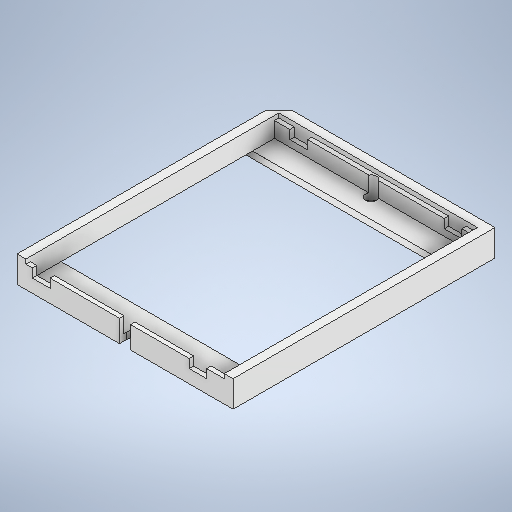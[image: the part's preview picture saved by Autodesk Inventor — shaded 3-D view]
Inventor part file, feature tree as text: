
AUTODESK INVENTOR PART (.ipt)
format: ipt  version: 2025 (Build 290162000, 162)  size: 386,560 bytes
history: native  units: in
note: dims shown in document units (in); Inventor stores cm internally (conversion verified against a paired STEP export)
features: extrude x11, sketch x10
ambient origin geometry x8: Origin, YZ Plane, XZ Plane, XY Plane, X Axis, Y Axis, Z Axis, Center Point
bodies: Solid1 (feature_tree)
feature tree (21):
  extrude  "Extrusion1"  Depth=1.9331in
  extrude  "Extrusion2"  Depth=0.0787in
  extrude  "Extrusion3"  Depth=0.0394in TaperAngle=0.0deg
  extrude  "Extrusion7"  Depth=2.2638in
  extrude  "Extrusion8"  Depth=0.0394in
  extrude  "Extrusion9"  Depth=0.0984in
  extrude  "Extrusion10"  Depth=0.0984in
  extrude  "Extrusion11"  TaperAngle=0.0deg  [1 undecoded]
  sketch  "Sketch17"  dims[d48=0.0394in d49=0.1181in]
  extrude  "Extrusion13"  Depth=0.1181in
  extrude  "Extrusion14"  Depth=0.3937in TaperAngle=0.0deg
  extrude  "Extrusion15"  Depth=0.1575in
  sketch  "Sketch1"  dims[d0=2.4606in d1=1.9331in]
  sketch  "Sketch2"  dims[d2=0.2362in d3=0.0in d4=0.0787in]
  sketch  "Sketch3"  dims[d5=0.0787in d6=0.0394in d7=0.0in]
  sketch  "Sketch9"  dims[d9=0.1378in d10=0.0in d36=2.2638in]
  sketch  "Sketch10"  dims[d37=0.0in d38=0.0in d39=0.0394in]
  sketch  "Sketch11"  dims[d40=0.3937in d41=0.0in d42=0.0984in]
  sketch  "Sketch12"  dims[d43=0.0984in d44=2.1378in]
  sketch  "Sketch13"  dims[d45=1.0886in d46=0.0in d47=0.0in]
  sketch  "Sketch18"  dims[d50=0.1181in d51=0.3937in d52=0.0in d53=0.1575in d54=0.1575in d55=0.0591in d56=0.1575in d57=0.1378in d58=0.0984in d59=0.1575in d60=0.1575in d61=0.0787in d62=0.0in d69=0.315in d72=45.0deg d73=45.0deg d75=45.0deg d76=45.0deg d77=0.315in d78=1.7717in d79=0.0in d80=0.1614in d81=0.0in d82=0.1614in d83=0.0in d70=0.0344in d71=0.0197in]
note: 1 required parameter value undecoded (feature->parameter linkage not recoverable at this tier; creation-order binding heuristic only, values carry confidence <= 0.55)
